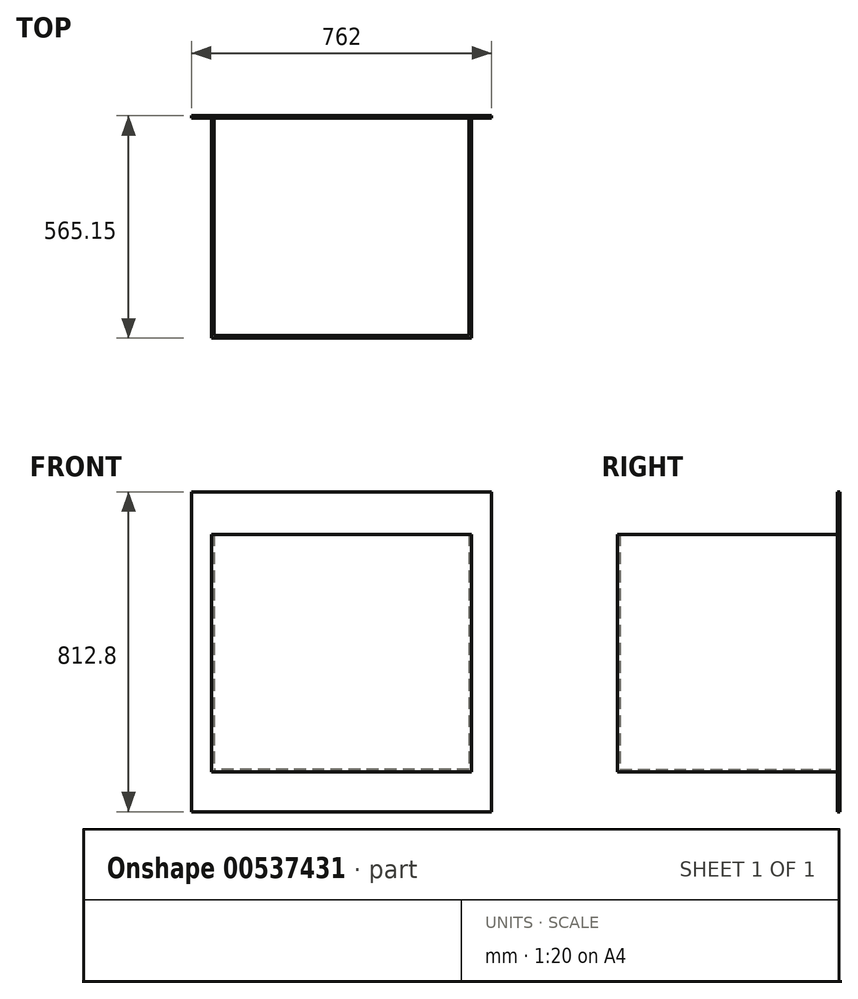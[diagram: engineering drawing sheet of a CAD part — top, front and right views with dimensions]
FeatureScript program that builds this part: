
annotation { "Feature Type Name" : "Feature", "Feature Type Description" : "" }
export const myFeature = defineFeature(function(context is Context, id is Id, definition is map)
    precondition{}
    {
        {
            var Q0;
            Q0=qCreatedBy(makeId("Front.planeOp"),FACE);
            var sketch = newSketch(context, id + "F0", { "sketchPlane" : qUnion([Q0])});
            skLineSegment(sketch, "E0.bottom", {"start": v(381, 406.4) * mm, "end": v(-381, 406.4) * mm});
            skLineSegment(sketch, "E0.top", {"start": v(381, -406.4) * mm, "end": v(-381, -406.4) * mm});
            skLineSegment(sketch, "E0.left", {"start": v(381, 406.4) * mm, "end": v(381, -406.4) * mm});
            skLineSegment(sketch, "E0.right", {"start": v(-381, 406.4) * mm, "end": v(-381, -406.4) * mm});
            skPoint(sketch, "E0.middle", {"position": v(0, 0) * mm});
            skSolve(sketch);
        }
        {
            var Q0;
            Q0=makeQuery(id+"F0.imprint","IMPRINT",FACE,{"disambiguationData":[TD([[makeQuery(id+"F0.imprint","IMPRINT",EDGE,{"derivedFrom":sQuery(id+"F0.wireOp",EDGE,"E0.bottom")}),1.0]])]});
            extrude(context, id + "F1", {"entities" : qUnion([Q0]), "depth" : 6.35 * mm, "offsetDistance" : 25.4 * mm});
        }
        {
            var Q0;
            Q0=makeQuery(id+"F1.opExtrude","CAP_FACE",FACE,{"disambiguationData":[OSD([sQuery(id+"F0.wireOp",EDGE,"E0.bottom"),sQuery(id+"F0.wireOp",EDGE,"E0.top"),sQuery(id+"F0.wireOp",EDGE,"E0.left"),sQuery(id+"F0.wireOp",EDGE,"E0.right")])],"isStart":false});
            var sketch = newSketch(context, id + "F2", { "sketchPlane" : qUnion([Q0])});
            skLineSegment(sketch, "E1.top", {"start": v(330.2, -304.8) * mm, "end": v(-330.2, -304.8) * mm});
            skLineSegment(sketch, "E1.left", {"start": v(330.2, 304.8) * mm, "end": v(330.2, -304.8) * mm});
            skLineSegment(sketch, "E1.right", {"start": v(-330.2, 298.45) * mm, "end": v(-330.2, -304.8) * mm});
            skPoint(sketch, "E1.middle", {"position": v(0, 0) * mm});
            skLineSegment(sketch, "E2.0", {"start": v(-323.85, 298.45) * mm, "end": v(-323.85, -298.45) * mm});
            skLineSegment(sketch, "E2.2", {"start": v(323.85, 298.45) * mm, "end": v(323.85, -298.45) * mm});
            skLineSegment(sketch, "E2.3", {"start": v(323.85, -298.45) * mm, "end": v(-323.85, -298.45) * mm});
            skLineSegment(sketch, "E3", {"start": v(323.85, 298.45) * mm, "end": v(330.2, 298.45) * mm});
            skLineSegment(sketch, "E4", {"start": v(-323.85, 298.45) * mm, "end": v(-330.2, 298.45) * mm});
            skPoint(sketch, "E1.bottom.end.orphan", {"position": v(-330.2, 304.8) * mm});
            skSolve(sketch);
        }
        {
            var Q0;
            {var subQ1=sQuery(id+"F2.wireOp",EDGE,"E1.top");Q0=makeQuery(id+"F2.imprint","IMPRINT",FACE,{"disambiguationData":[TD([[makeQuery(id+"F2.imprint","IMPRINT",EDGE,{"derivedFrom":subQ1}),-1.0]])]});}
            extrude(context, id + "F3", {"entities" : qUnion([Q0]), "operationType" : NewBodyOperationType.ADD, "depth" : 552.45 * mm, "offsetDistance" : 25.4 * mm});
        }
        {
            var Q0;
            Q0=makeQuery(id+"F3.opExtrude","CAP_FACE",FACE,{"disambiguationData":[OSD([sQuery(id+"F2.wireOp",EDGE,"E1.top"),sQuery(id+"F2.wireOp",EDGE,"E1.left"),sQuery(id+"F2.wireOp",EDGE,"E1.right"),sQuery(id+"F2.wireOp",EDGE,"E2.0"),sQuery(id+"F2.wireOp",EDGE,"E2.2"),sQuery(id+"F2.wireOp",EDGE,"E2.3"),sQuery(id+"F2.wireOp",EDGE,"E3"),sQuery(id+"F2.wireOp",EDGE,"E4")])],"isStart":false});
            var sketch = newSketch(context, id + "F4", { "sketchPlane" : qUnion([Q0])});
            skLineSegment(sketch, "E5.bottom", {"start": v(-330.2, -304.8) * mm, "end": v(330.2, -304.8) * mm});
            skLineSegment(sketch, "E5.top", {"start": v(-330.2, 298.45) * mm, "end": v(330.2, 298.45) * mm});
            skLineSegment(sketch, "E5.left", {"start": v(-330.2, -304.8) * mm, "end": v(-330.2, 298.45) * mm});
            skLineSegment(sketch, "E5.right", {"start": v(330.2, -304.8) * mm, "end": v(330.2, 298.45) * mm});
            skSolve(sketch);
        }
        {
            var Q0;
            Q0=makeQuery(id+"F4.imprint","IMPRINT",FACE,{"disambiguationData":[TD([[makeQuery(id+"F4.imprint","IMPRINT",EDGE,{"derivedFrom":sQuery(id+"F4.wireOp",EDGE,"E5.bottom")}),-1.0]])]});
            var Q1;
            {var subQ1=makeQuery(id+"F3.opExtrude","CAP_EDGE",EDGE,{"disambiguationData":[OSD([sQuery(id+"F2.wireOp",EDGE,"E2.0")])],"isStart":false});Q1=makeQuery(id+"F4.imprint","IMPRINT",FACE,{"disambiguationData":[TD([[makeQuery(id+"F4.imprint","IMPRINT",EDGE,{"derivedFrom":subQ1}),1.0]])]});}
            extrude(context, id + "F5", {"entities" : qUnion([Q0, Q1]), "operationType" : NewBodyOperationType.ADD, "depth" : 6.35 * mm, "offsetDistance" : 25.4 * mm});
        }
    });
